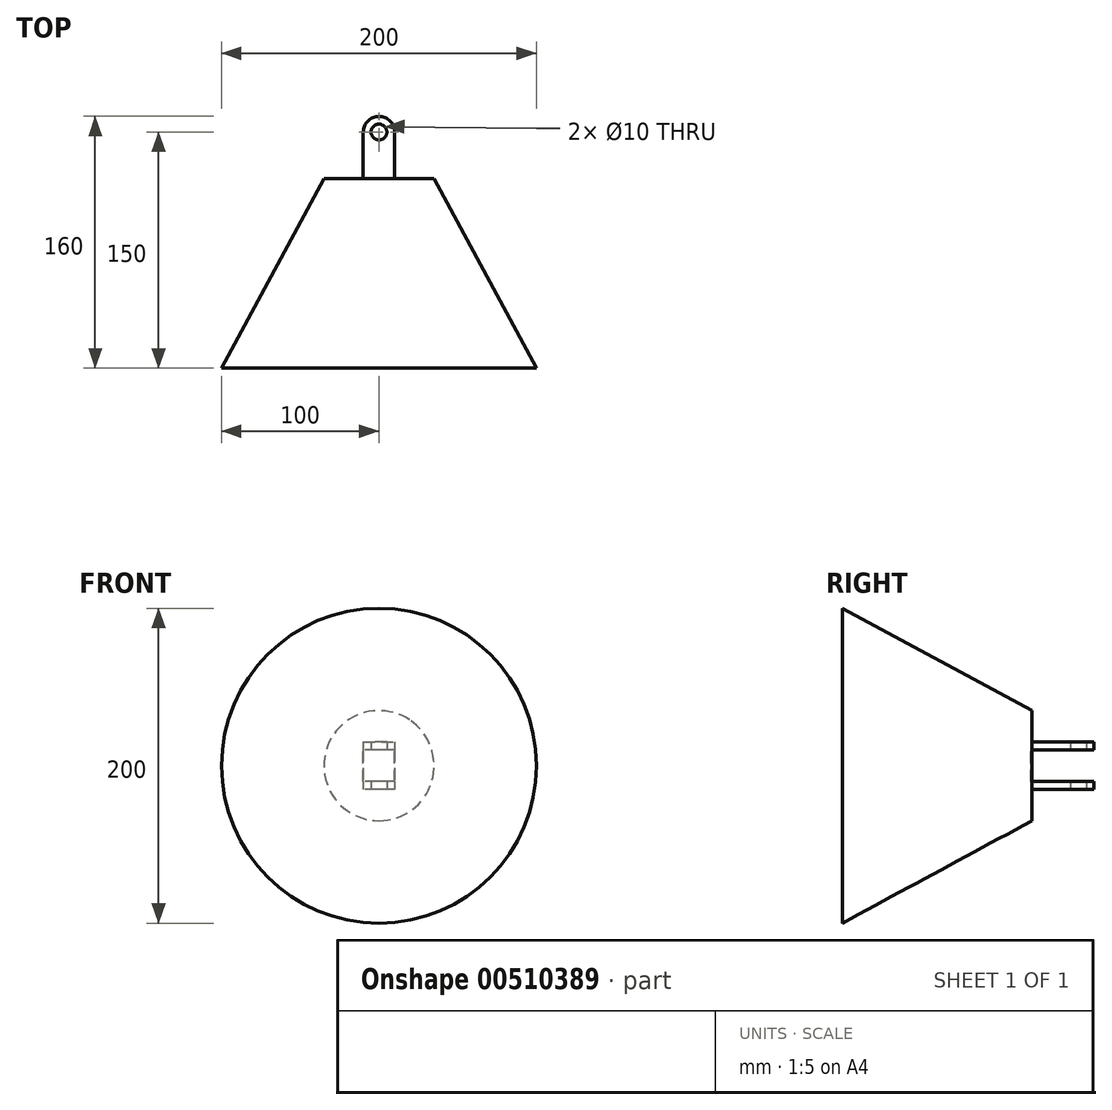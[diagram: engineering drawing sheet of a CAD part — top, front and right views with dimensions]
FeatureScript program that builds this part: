
annotation { "Feature Type Name" : "Feature", "Feature Type Description" : "" }
export const myFeature = defineFeature(function(context is Context, id is Id, definition is map)
    precondition{}
    {
        {
            var Q0;
            Q0=qCreatedBy(makeId("Top.planeOp"),FACE);
            var sketch = newSketch(context, id + "F0", { "sketchPlane" : qUnion([Q0])});
            skLineSegment(sketch, "E0", {"start": v(0, 0) * mm, "end": v(0, 120) * mm, "construction": true});
            skLineSegment(sketch, "E1", {"start": v(0, 0) * mm, "end": v(-100, 0) * mm});
            skLineSegment(sketch, "E2", {"start": v(-100, 0) * mm, "end": v(-35, 120.5) * mm});
            skLineSegment(sketch, "E3", {"start": v(-35, 120.5) * mm, "end": v(0, 120) * mm});
            skLineSegment(sketch, "E4", {"start": v(0, 0) * mm, "end": v(0, 120) * mm});
            skSolve(sketch);
        }
        {
            var Q0;
            Q0=makeQuery(id+"F0.imprint","IMPRINT",FACE,{"disambiguationData":[TD([[makeQuery(id+"F0.imprint","IMPRINT",EDGE,{"derivedFrom":sQuery(id+"F0.wireOp",EDGE,"E1")}),-1.0]])]});
            var Q1;
            Q1=sQuery(id+"F0.wireOp",EDGE,"E4");
            revolve(context, id + "F1", {"entities" : qUnion([Q0]), "axis" : qUnion([Q1]), "revolveType" : RevolveType.FULL});
        }
        {
            var Q0;
            Q0=qCreatedBy(makeId("Top.planeOp"),FACE);
            var sketch = newSketch(context, id + "F2", { "sketchPlane" : qUnion([Q0])});
            skLineSegment(sketch, "E5", {"start": v(0, 0) * mm, "end": v(0, 256.3) * mm, "construction": true});
            skLineSegment(sketch, "E6.top", {"start": v(0, 120) * mm, "end": v(-10, 120) * mm});
            skLineSegment(sketch, "E6.left", {"start": v(0, 150) * mm, "end": v(0, 120) * mm});
            skLineSegment(sketch, "E6.right", {"start": v(-10, 150) * mm, "end": v(-10, 120) * mm});
            skLineSegment(sketch, "E7.MirrorCS", {"start": v(10, 150) * mm, "end": v(10, 120) * mm});
            skArc(sketch, "E8", {"start": v(10, 150) * mm, "mid": v(0, 160) * mm, "end": v(-10, 150) * mm});
            skCircle(sketch, "E9", {"center": v(0, 150) * mm, "radius": 5 * mm});
            skPoint(sketch, "E10.MirrorCS.end.orphan", {"position": v(10, 150) * mm});
            skLineSegment(sketch, "E11", {"start": v(0, 120) * mm, "end": v(10, 120) * mm});
            skSolve(sketch);
        }
        {
            var Q0;
            Q0 = qSketchRegion(id + "F2", true);
            extrude(context, id + "F3", {"entities" : qUnion([Q0]), "operationType" : NewBodyOperationType.ADD, "endBound" : BoundingType.SYMMETRIC, "depth" : 30 * mm});
        }
        {
            var Q0;
            Q0=qCreatedBy(makeId("Top.planeOp"),FACE);
            var sketch = newSketch(context, id + "F4", { "sketchPlane" : qUnion([Q0])});
            skLineSegment(sketch, "E12", {"start": v(0, 0) * mm, "end": v(0, 163.93) * mm, "construction": true});
            skLineSegment(sketch, "E13.bottom", {"start": v(0, 120) * mm, "end": v(-10, 120) * mm});
            skLineSegment(sketch, "E13.left", {"start": v(0, 120) * mm, "end": v(0, 150) * mm});
            skLineSegment(sketch, "E13.right", {"start": v(-10, 120) * mm, "end": v(-10, 150) * mm});
            skLineSegment(sketch, "E14.MirrorCS", {"start": v(10, 120) * mm, "end": v(10, 150) * mm});
            skLineSegment(sketch, "E15.MirrorCS", {"start": v(0, 120) * mm, "end": v(10, 120) * mm});
            skArc(sketch, "E16", {"start": v(10, 150) * mm, "mid": v(0, 160) * mm, "end": v(-10, 150) * mm});
            skCircle(sketch, "E17", {"center": v(0, 150) * mm, "radius": 5 * mm});
            skSolve(sketch);
        }
        {
            var Q0;
            Q0 = qSketchRegion(id + "F4", true);
            extrude(context, id + "F5", {"entities" : qUnion([Q0]), "operationType" : NewBodyOperationType.REMOVE, "endBound" : BoundingType.SYMMETRIC, "oppositeDirection" : true, "depth" : 20 * mm});
        }
    });
